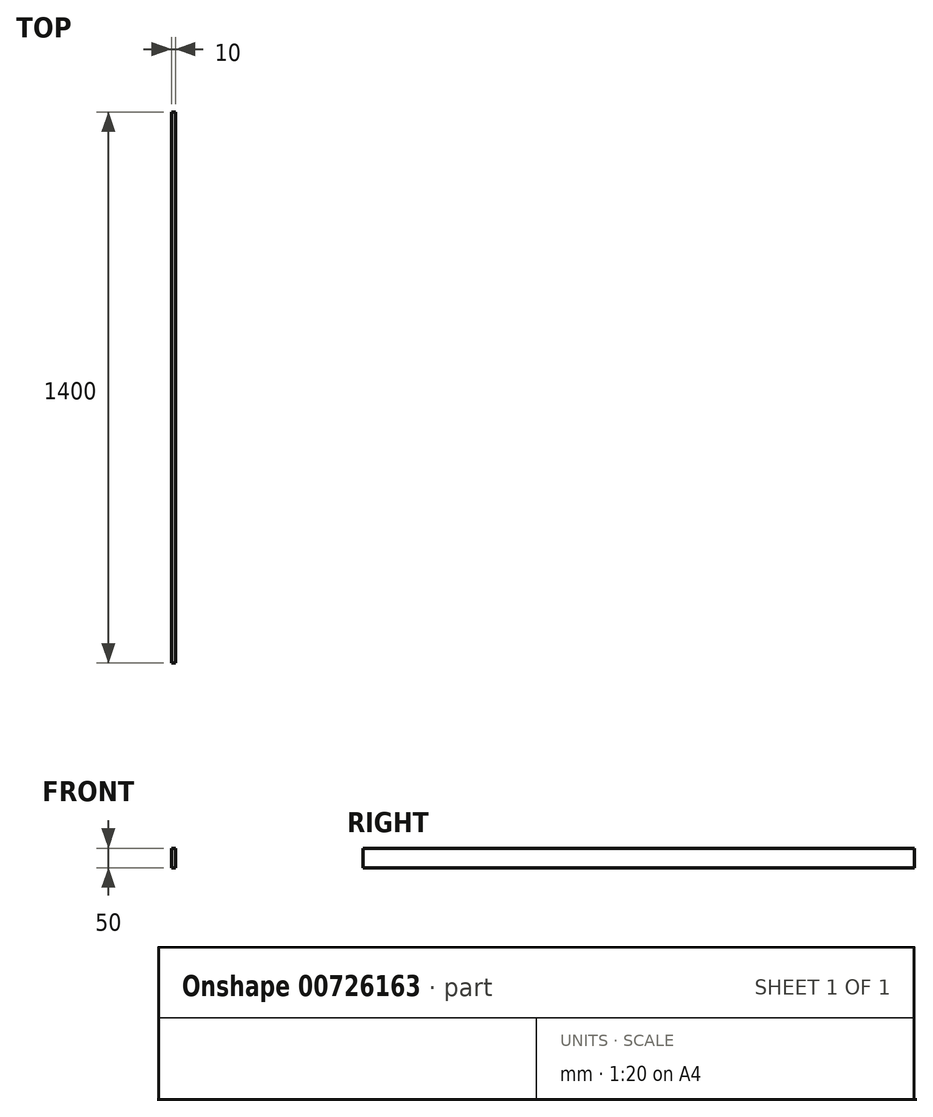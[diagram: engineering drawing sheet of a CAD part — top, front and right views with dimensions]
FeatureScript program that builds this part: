
annotation { "Feature Type Name" : "Feature", "Feature Type Description" : "" }
export const myFeature = defineFeature(function(context is Context, id is Id, definition is map)
    precondition{}
    {
        {
            var Q0;
            Q0=qCreatedBy(makeId("Right.planeOp"),FACE);
            var sketch = newSketch(context, id + "F0", { "sketchPlane" : qUnion([Q0])});
            skLineSegment(sketch, "E0.bottom", {"start": v(-700, 25) * mm, "end": v(700, 25) * mm});
            skLineSegment(sketch, "E0.top", {"start": v(-700, -25) * mm, "end": v(700, -25) * mm});
            skLineSegment(sketch, "E0.left", {"start": v(-700, 25) * mm, "end": v(-700, -25) * mm});
            skLineSegment(sketch, "E0.right", {"start": v(700, 25) * mm, "end": v(700, -25) * mm});
            skLineSegment(sketch, "E1", {"start": v(-700, 0) * mm, "end": v(700, 0) * mm, "construction": true});
            skSolve(sketch);
        }
        {
            var Q0;
            Q0 = qSketchRegion(id + "F0", true);
            extrude(context, id + "F1", {"entities" : qUnion([Q0]), "depth" : 10 * mm, "offsetDistance" : 25 * mm});
        }
    });
